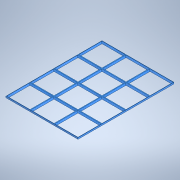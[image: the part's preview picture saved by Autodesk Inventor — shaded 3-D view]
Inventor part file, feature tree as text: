
AUTODESK INVENTOR PART (.ipt)
format: ipt  version: 2021 (Build 250183000, 183)  size: 190,464 bytes
history: native  units: mm
features: extrude x3, sketch x3
ambient origin geometry x8: Origin, YZ Plane, XZ Plane, XY Plane, X Axis, Y Axis, Z Axis, Center Point
bodies: Solid1 (feature_tree)
feature tree (6):
  extrude  "Extrusion1"  Depth=5.0mm
  extrude  "Extrusion2"  Depth=3.0mm TaperAngle=0.0deg
  extrude  "Extrusion3"  Depth=0.872665mm
  sketch  "Sketch4"  dims[d70=40.0mm d72=50.0mm d73=30.0mm d75=50.0mm d78=5.0mm d79=-5.235988mm]
  sketch  "Sketch5"  dims[d80=3.0mm d81=0.0mm d82=10.0mm d83=0.0mm]
  sketch  "Sketch7"  dims[d84=0.5mm d85=0.872665mm d86=0.5mm d87=0.872665mm]
